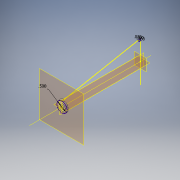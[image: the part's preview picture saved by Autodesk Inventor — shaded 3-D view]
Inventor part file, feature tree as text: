
AUTODESK INVENTOR PART (.ipt)
format: ipt  version: 2018 (Build 220112000, 112)  size: 332,288 bytes
history: native  units: in
note: dims shown in document units (in); Inventor stores cm internally (conversion verified against a paired STEP export)
features: sketch x5, other x2, helix x2, plane x1, loft x1, hole x1, extrude x1, projected_geometry x1
ambient origin geometry x8: Origin, YZ Plane, XZ Plane, XY Plane, X Axis, Y Axis, Z Axis, Center Point
bodies: Solid1 (feature_tree)
feature tree (14):
  sketch  "Sketch1"  dims[d0=2.0in d2=3.9in]
  plane  "Work Plane1"
  loft  "Loft1"
  other  "Work Point1"
  hole  "Hole1"  [1 undecoded]
  other  "Work Axis2"
  sketch  "Sketch6"  dims[d65=1.0in d66=1.0in d11=0.181in d12=0.75in d13=0.375in d14=0.25in d15=0.5635in d16=1.0in d17=0.8108in d41=0.1in]
  helix  "Coil3"  [1 undecoded]
  helix  "Coil4"  [1 undecoded]
  extrude  "Extrusion2"  Depth=0.02in
  sketch  "Sketch9"  dims[d44=0.13in d45=1.0in d46=11.811in d47=-0.0739in d48=90.0deg d49=90.0deg d50=0.0in d51=0.0in d52=0.13in d53=1.0in d54=11.811in d55=0.0756in d56=90.0deg d57=90.0deg d58=0.0in d59=0.0in d60=3.775in d61=3.0in d62=0.0in]
  sketch  "Sketch2"  dims[d3=0.5in d5=0.0in d6=90.0deg d7=0.0in d8=90.0deg]
  projected_geometry  "Projected Loop1"
  sketch  "Sketch8"  dims[d42=0.1in d43=0.02in]
note: 3 required parameter values undecoded (feature->parameter linkage not recoverable at this tier; creation-order binding heuristic only, values carry confidence <= 0.55)
